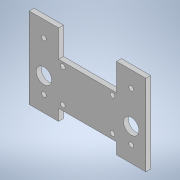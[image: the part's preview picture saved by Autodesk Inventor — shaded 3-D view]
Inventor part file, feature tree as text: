
AUTODESK INVENTOR PART (.ipt)
format: ipt  version: 2021 (Build 250183000, 183)  size: 148,480 bytes
history: native  units: in
note: dims shown in document units (in); Inventor stores cm internally (conversion verified against a paired STEP export)
features: reference x21, other x5, extrude x4, sketch x4, plane x2
ambient origin geometry x8: Origin, YZ Plane, XZ Plane, XY Plane, X Axis, Y Axis, Z Axis, Center Point
bodies: Solid1 (feature_tree)
feature tree (36):
  plane  "Work Plane1"
  extrude  "Extrusion1"  Depth=0.1181in TaperAngle=0.0deg
  sketch  "Sketch2"  dims[d8=0.1142in d9=0.1142in]
  plane  "Work Plane2"
  extrude  "Extrusion2"  Depth=0.1142in
  extrude  "Extrusion3"  Depth=0.1142in
  extrude  "Extrusion4"  Depth=0.391in
  sketch  "Sketch1"  dims[d4=0.1181in d5=0.0in d6=0.1181in d7=0.0in]
  reference  "Reference2"
  reference  "Reference3"
  reference  "Reference4"
  reference  "Reference5"
  reference  "Reference6"
  reference  "Reference7"
  reference  "Reference8"
  reference  "Reference9"
  reference  "Reference10"
  reference  "Reference11"
  reference  "Reference12"
  reference  "Reference13"
  reference  "Reference14"
  reference  "Reference15"
  reference  "Reference16"
  reference  "Reference17"
  reference  "Reference18"
  sketch  "Sketch3"  dims[d10=0.1142in d11=0.1142in]
  reference  "Reference19"
  reference  "Reference20"
  reference  "Reference21"
  reference  "Reference22"
  sketch  "Sketch4"  dims[d12=0.0in d13=0.0in d14=0.391in d15=0.3754in d16=0.3754in d17=0.0in d18=0.0in]
  parser-record x1  (decoder bookkeeping rows leaked as tree rows — omitted from the tree; the rows remain in map.json)
  other  "assembly.iam"
  other  "DIN_mount:7"
  other  "DIN_mount:8"
  other  "GPS_ublox_board:1"
note: 1 file-system path scrubbed to <path> (originals preserved in map.json)
